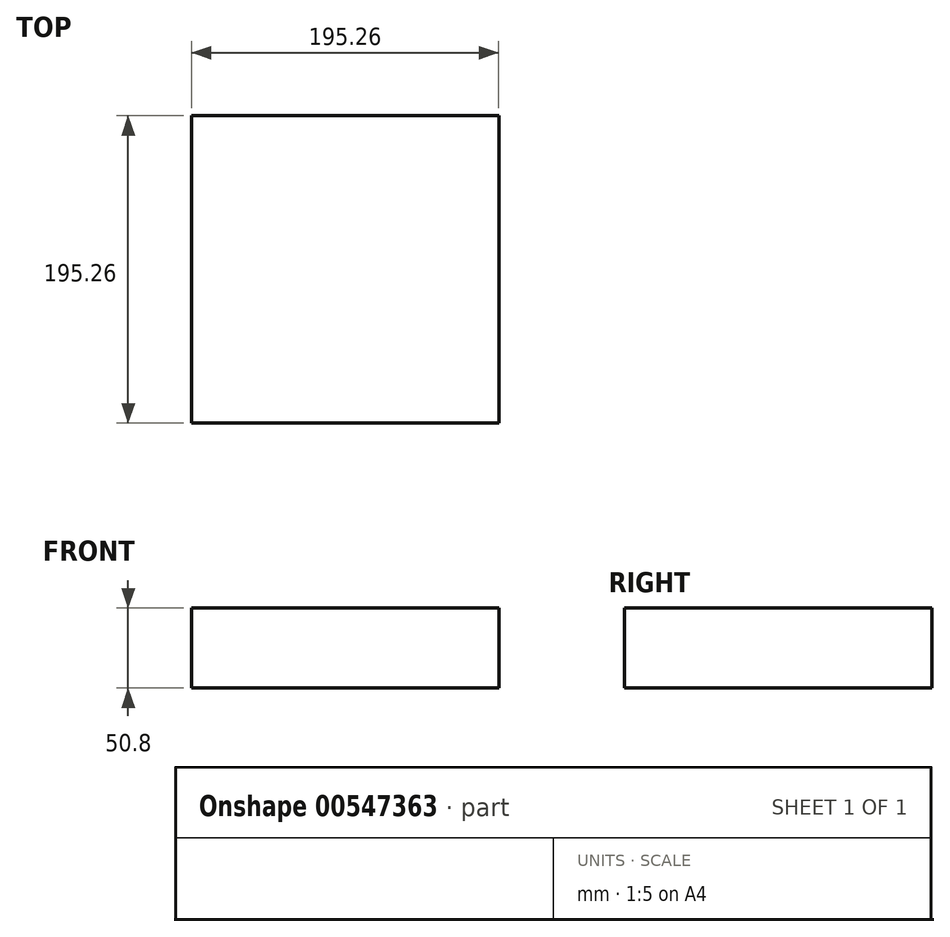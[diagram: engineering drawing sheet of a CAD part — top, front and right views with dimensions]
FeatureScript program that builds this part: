
annotation { "Feature Type Name" : "Feature", "Feature Type Description" : "" }
export const myFeature = defineFeature(function(context is Context, id is Id, definition is map)
    precondition{}
    {
        {
            var Q0;
            Q0=qCreatedBy(makeId("Top.planeOp"),FACE);
            var sketch = newSketch(context, id + "F0", { "sketchPlane" : qUnion([Q0])});
            skLineSegment(sketch, "E0.bottom", {"start": v(97.63, 97.63) * mm, "end": v(-97.63, 97.63) * mm});
            skLineSegment(sketch, "E0.top", {"start": v(97.63, -97.63) * mm, "end": v(-97.63, -97.63) * mm});
            skLineSegment(sketch, "E0.left", {"start": v(97.63, 97.63) * mm, "end": v(97.63, -97.63) * mm});
            skLineSegment(sketch, "E0.right", {"start": v(-97.63, 97.63) * mm, "end": v(-97.63, -97.63) * mm});
            skPoint(sketch, "E0.middle", {"position": v(0, 0) * mm});
            skSolve(sketch);
        }
        {
            var Q0;
            Q0=makeQuery(id+"F0.imprint","IMPRINT",FACE,{"disambiguationData":[TD([[makeQuery(id+"F0.imprint","IMPRINT",EDGE,{"derivedFrom":sQuery(id+"F0.wireOp",EDGE,"E0.bottom")}),1.0]])]});
            extrude(context, id + "F1", {"entities" : qUnion([Q0]), "depth" : 50.8 * mm, "offsetDistance" : 25.4 * mm});
        }
    });
